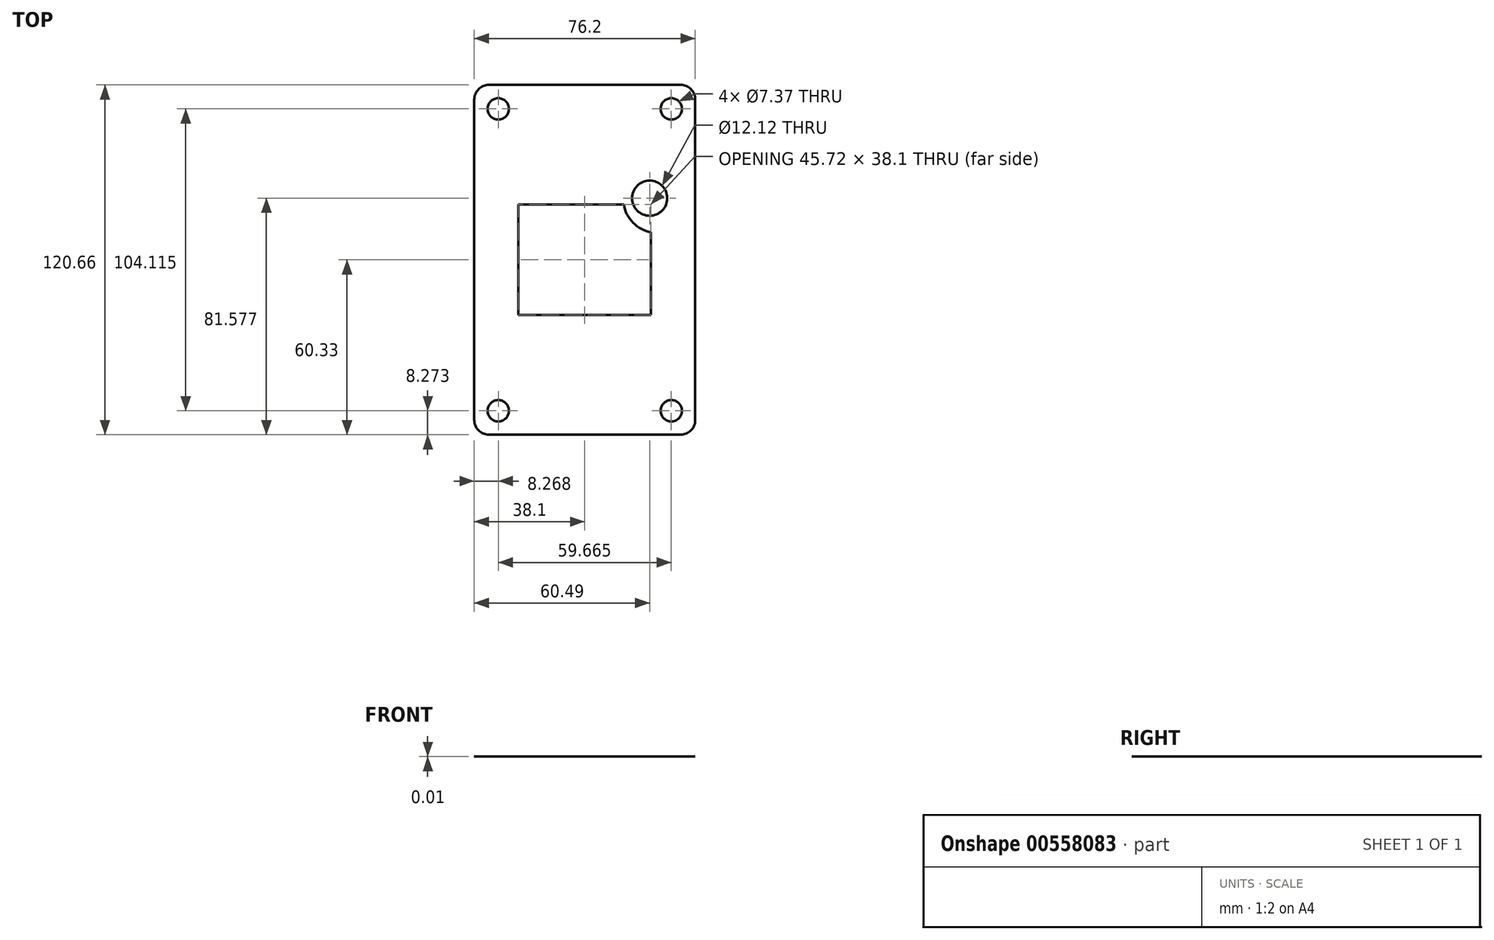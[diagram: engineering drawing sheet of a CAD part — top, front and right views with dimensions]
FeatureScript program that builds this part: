
annotation { "Feature Type Name" : "Feature", "Feature Type Description" : "" }
export const myFeature = defineFeature(function(context is Context, id is Id, definition is map)
    precondition{}
    {
        {
            var Q0;
            Q0=qCreatedBy(makeId("Top.planeOp"),FACE);
            var sketch = newSketch(context, id + "F0", { "sketchPlane" : qUnion([Q0])});
            skLineSegment(sketch, "E0.bottom", {"start": v(-38.1, 60.33) * mm, "end": v(38.1, 60.33) * mm});
            skLineSegment(sketch, "E0.top", {"start": v(-38.1, -60.33) * mm, "end": v(38.1, -60.33) * mm});
            skLineSegment(sketch, "E0.left", {"start": v(-38.1, 60.33) * mm, "end": v(-38.1, -60.33) * mm});
            skLineSegment(sketch, "E0.right", {"start": v(38.1, 60.33) * mm, "end": v(38.1, -60.33) * mm});
            skCircle(sketch, "E1", {"center": v(-29.83, 52.06) * mm, "radius": 3.68 * mm});
            skCircle(sketch, "E2", {"center": v(29.83, 52.06) * mm, "radius": 3.68 * mm});
            skCircle(sketch, "E3", {"center": v(-29.83, -52.06) * mm, "radius": 3.68 * mm});
            skCircle(sketch, "E4", {"center": v(29.83, -52.06) * mm, "radius": 3.68 * mm});
            skCircle(sketch, "E5", {"center": v(0, 0) * mm, "radius": 12.7 * mm});
            skCircle(sketch, "E6", {"center": v(22.4, 21.25) * mm, "radius": 6.06 * mm});
            skLineSegment(sketch, "E7.bottom", {"start": v(-29.83, -52.06) * mm, "end": v(29.83, -52.06) * mm, "construction": true});
            skLineSegment(sketch, "E7.top", {"start": v(-29.83, 52.06) * mm, "end": v(29.83, 52.06) * mm, "construction": true});
            skLineSegment(sketch, "E7.left", {"start": v(-29.83, -52.06) * mm, "end": v(-29.83, 52.06) * mm, "construction": true});
            skLineSegment(sketch, "E7.right", {"start": v(29.83, -52.06) * mm, "end": v(29.83, 52.06) * mm, "construction": true});
            skSolve(sketch);
        }
        {
            var Q0;
            Q0=makeQuery(id+"F0.imprint","IMPRINT",FACE,{"disambiguationData":[TD([[makeQuery(id+"F0.imprint","IMPRINT",EDGE,{"derivedFrom":sQuery(id+"F0.wireOp",EDGE,"E0.bottom")}),-1.0]])]});
            extrude(context, id + "F1", {"entities" : qUnion([Q0]), "depth" : 1 / 101.6 * mm, "offsetDistance" : 25.4 * mm});
        }
        {
            var Q0;
            Q0=makeQuery(id+"F1.opExtrude","SWEPT_EDGE",EDGE,{"disambiguationData":[OSD([sQuery(id+"F0.wireOp",EDGE,"E0.top"),sQuery(id+"F0.wireOp",EDGE,"E0.right")])]});
            var Q1;
            Q1=makeQuery(id+"F1.opExtrude","SWEPT_EDGE",EDGE,{"disambiguationData":[OSD([sQuery(id+"F0.wireOp",EDGE,"E0.bottom"),sQuery(id+"F0.wireOp",EDGE,"E0.left")])]});
            var Q2;
            Q2=makeQuery(id+"F1.opExtrude","SWEPT_EDGE",EDGE,{"disambiguationData":[OSD([sQuery(id+"F0.wireOp",EDGE,"E0.bottom"),sQuery(id+"F0.wireOp",EDGE,"E0.right")])]});
            var Q3;
            Q3=makeQuery(id+"F1.opExtrude","SWEPT_EDGE",EDGE,{"disambiguationData":[OSD([sQuery(id+"F0.wireOp",EDGE,"E0.top"),sQuery(id+"F0.wireOp",EDGE,"E0.left")])]});
            fillet(context, id + "F2", {"entities" : qUnion([Q0, Q1, Q2, Q3]), "radius" : 5.08 * mm, "tangentPropagation" : true, "allowEdgeOverflow" : false});
        }
        {
            var Q0;
            Q0=makeQuery(id+"F1.opExtrude","CAP_FACE",FACE,{"disambiguationData":[OSD([sQuery(id+"F0.wireOp",EDGE,"E0.bottom"),sQuery(id+"F0.wireOp",EDGE,"E0.top"),sQuery(id+"F0.wireOp",EDGE,"E0.left"),sQuery(id+"F0.wireOp",EDGE,"E0.right"),sQuery(id+"F0.wireOp",EDGE,"E1"),sQuery(id+"F0.wireOp",EDGE,"E2"),sQuery(id+"F0.wireOp",EDGE,"E3"),sQuery(id+"F0.wireOp",EDGE,"E4"),sQuery(id+"F0.wireOp",EDGE,"E5"),sQuery(id+"F0.wireOp",EDGE,"E6")])],"isStart":true});
            var sketch = newSketch(context, id + "F3", { "sketchPlane" : qUnion([Q0])});
            skLineSegment(sketch, "E8.bottom", {"start": v(14.44, 19.05) * mm, "end": v(-22.86, 19.05) * mm});
            skLineSegment(sketch, "E8.top", {"start": v(13.48, -19.05) * mm, "end": v(-22.86, -19.05) * mm});
            skLineSegment(sketch, "E8.right", {"start": v(-22.86, 19.05) * mm, "end": v(-22.86, -19.05) * mm});
            skLineSegment(sketch, "E9", {"start": v(14.44, 19.05) * mm, "end": v(22.86, 19.05) * mm});
            skLineSegment(sketch, "E10", {"start": v(22.86, 19.05) * mm, "end": v(22.86, -9.5) * mm});
            skArc(sketch, "E11", {"start": v(22.86, -9.5) * mm, "mid": v(16.65, -12.78) * mm, "end": v(13.48, -19.05) * mm});
            skSolve(sketch);
        }
        {
            var Q0;
            Q0=makeQuery(id+"F3.imprint","IMPRINT",FACE,{"disambiguationData":[TD([[makeQuery(id+"F3.imprint","IMPRINT",EDGE,{"derivedFrom":sQuery(id+"F3.wireOp",EDGE,"E8.bottom")}),1.0]])]});
            extrude(context, id + "F4", {"entities" : qUnion([Q0]), "operationType" : NewBodyOperationType.REMOVE, "oppositeDirection" : true, "depth" : 5.08 * mm, "offsetDistance" : 25.4 * mm});
        }
    });
